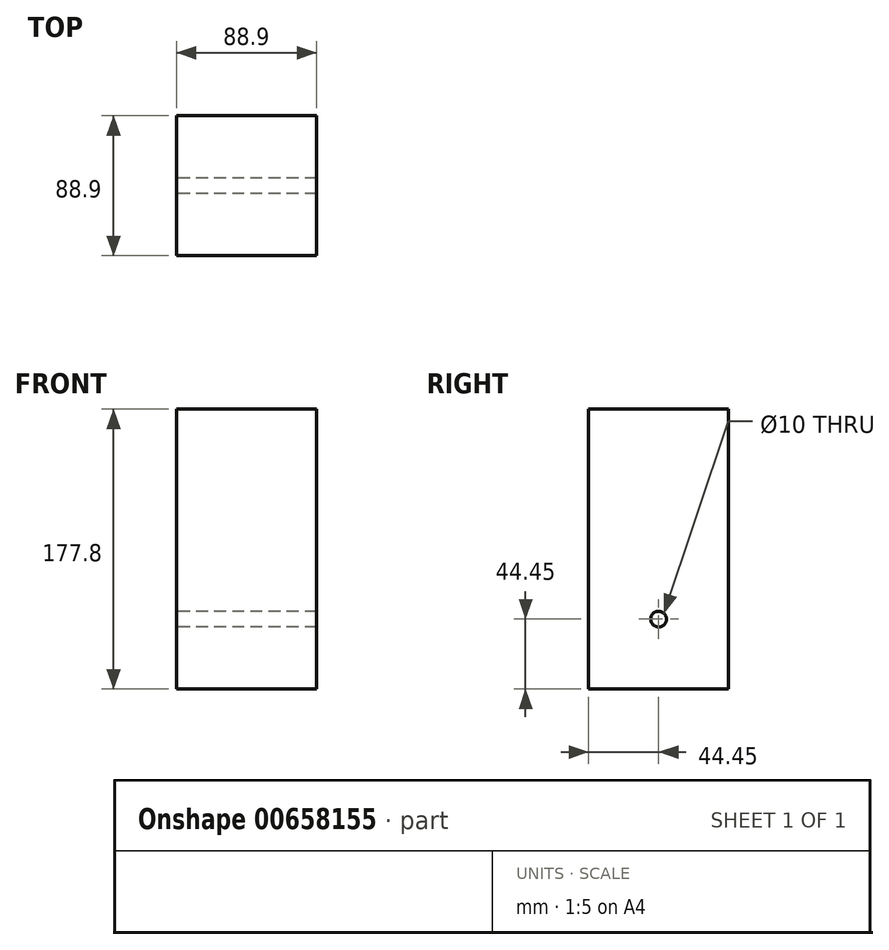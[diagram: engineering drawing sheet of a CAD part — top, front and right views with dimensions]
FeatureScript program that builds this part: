
annotation { "Feature Type Name" : "Feature", "Feature Type Description" : "" }
export const myFeature = defineFeature(function(context is Context, id is Id, definition is map)
    precondition{}
    {
        {
            var Q0;
            Q0=qCreatedBy(makeId("Front.planeOp"),FACE);
            var sketch = newSketch(context, id + "F0", { "sketchPlane" : qUnion([Q0])});
            skLineSegment(sketch, "E0.bottom", {"start": v(88.9, 177.8) * mm, "end": v(0, 177.8) * mm});
            skLineSegment(sketch, "E0.top", {"start": v(88.9, 0) * mm, "end": v(0, 0) * mm});
            skLineSegment(sketch, "E0.left", {"start": v(88.9, 177.8) * mm, "end": v(88.9, 0) * mm});
            skLineSegment(sketch, "E0.right", {"start": v(0, 177.8) * mm, "end": v(0, 0) * mm});
            skSolve(sketch);
        }
        {
            var Q0;
            Q0=makeQuery(id+"F0.imprint","IMPRINT",FACE,{"disambiguationData":[TD([[makeQuery(id+"F0.imprint","IMPRINT",EDGE,{"derivedFrom":sQuery(id+"F0.wireOp",EDGE,"E0.bottom")}),1.0]])]});
            extrude(context, id + "F1", {"entities" : qUnion([Q0]), "depth" : 88.9 * mm, "offsetDistance" : 25.4 * mm});
        }
        {
            var Q0;
            Q0=makeQuery(id+"F1.opExtrude","SWEPT_FACE",FACE,{"disambiguationData":[OSD([sQuery(id+"F0.wireOp",EDGE,"E0.right")])]});
            var sketch = newSketch(context, id + "F2", { "sketchPlane" : qUnion([Q0])});
            skPoint(sketch, "E1", {"position": v(44.45, 44.45) * mm});
            skSolve(sketch);
        }
        {
            var Q0;
            Q0=sQuery(id+"F2.wireOp",VERTEX,"E1");
            var Q1;
            Q1=makeQuery(id+"F1.opExtrude","SWEPT_BODY",BODY,{"disambiguationData":[OSD([sQuery(id+"F0.wireOp",EDGE,"E0.bottom"),sQuery(id+"F0.wireOp",EDGE,"E0.top"),sQuery(id+"F0.wireOp",EDGE,"E0.left"),sQuery(id+"F0.wireOp",EDGE,"E0.right")])]});
            hole(context, id + "F3", {"style" : HoleStyle.SIMPLE, "endStyle" : HoleEndStyle.THROUGH, "holeDiameter" : 10 * mm, "majorDiameter" : 6.35 * mm, "isTappedThrough" : true, "tappedDepth" : 12.7 * mm, "tapClearance" : 3, "locations" : qUnion([Q0]), "scope" : qUnion([Q1])});
        }
    });
